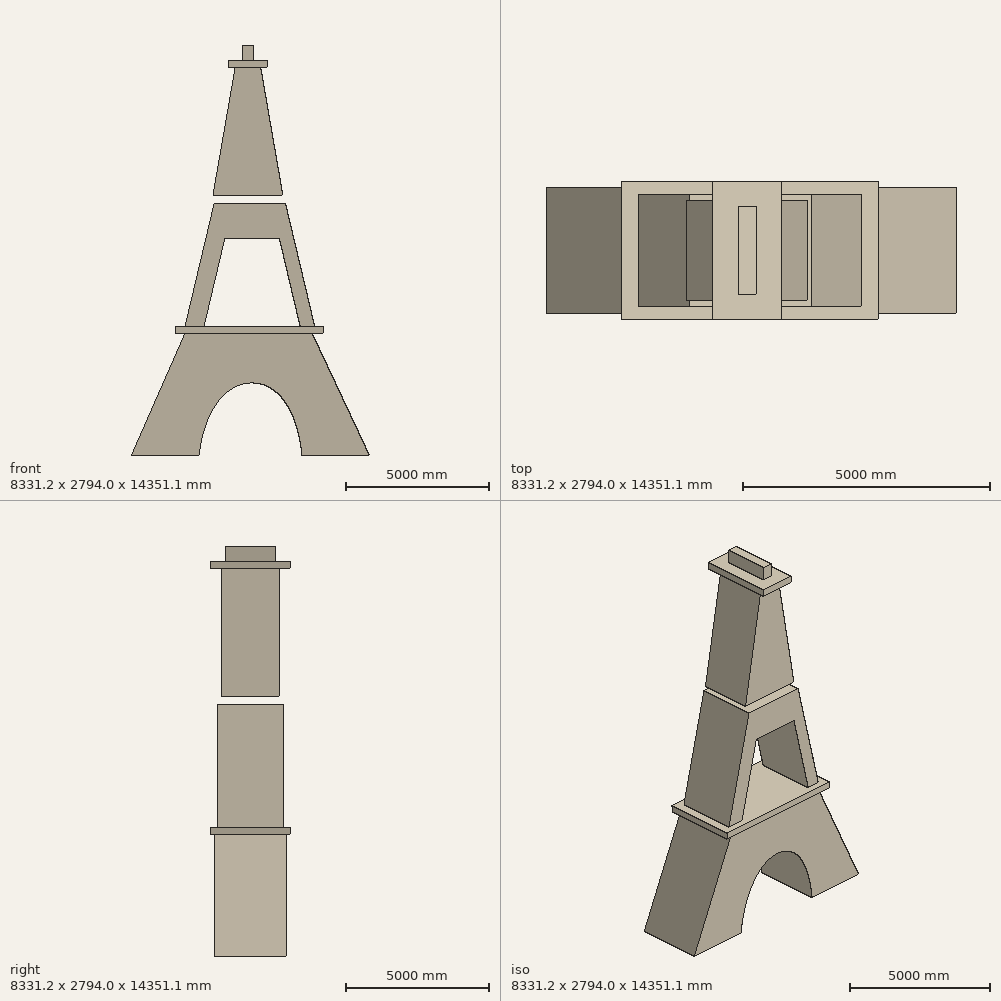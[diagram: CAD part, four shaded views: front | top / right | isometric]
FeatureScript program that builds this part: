
annotation { "Feature Type Name" : "Feature", "Feature Type Description" : "" }
export const myFeature = defineFeature(function(context is Context, id is Id, definition is map)
    precondition{}
    {
        {
            var Q0;
            Q0=qCreatedBy(makeId("Front.planeOp"),FACE);
            var sketch = newSketch(context, id + "F0", { "sketchPlane" : qUnion([Q0])});
            skLineSegment(sketch, "E0", {"start": v(0, 0) * mm, "end": v(-2362.2, 0) * mm});
            skLineSegment(sketch, "E1", {"start": v(3606.8, 0) * mm, "end": v(5969, 0) * mm});
            skFitSpline(sketch, "E2", {"points": [v(0, 0) * mm, v(1882.5, 2540) * mm, v(3606.8, 0) * mm], "startDerivative": vector(1303.2, 10552.75) * mm, "endDerivative": vector(1103.96, -10584.22) * mm});
            skLineSegment(sketch, "E3", {"start": v(-2362.2, 0) * mm, "end": v(-461.9, 4325.37) * mm});
            skLineSegment(sketch, "E4", {"start": v(-483.25, 4276.79) * mm, "end": v(3961.75, 4276.79) * mm});
            skLineSegment(sketch, "E5", {"start": v(3961.75, 4276.79) * mm, "end": v(5969, 0) * mm});
            skLineSegment(sketch, "E6", {"start": v(-832.7, 4530.55) * mm, "end": v(4374.3, 4530.55) * mm});
            skLineSegment(sketch, "E7", {"start": v(4374.3, 4530.55) * mm, "end": v(4374.3, 4276.79) * mm});
            skLineSegment(sketch, "E8", {"start": v(4374.3, 4276.79) * mm, "end": v(3961.75, 4276.79) * mm});
            skLineSegment(sketch, "E9", {"start": v(-483.25, 4276.79) * mm, "end": v(-821.6, 4276.79) * mm});
            skLineSegment(sketch, "E10", {"start": v(-821.6, 4276.79) * mm, "end": v(-832.7, 4530.55) * mm});
            skLineSegment(sketch, "E11", {"start": v(-483.25, 4530.55) * mm, "end": v(536.71, 8830.84) * mm});
            skLineSegment(sketch, "E12", {"start": v(4047.99, 4530.55) * mm, "end": v(3025.91, 8830.34) * mm});
            skLineSegment(sketch, "E13", {"start": v(536.71, 8830.84) * mm, "end": v(3025.91, 8830.34) * mm});
            skLineSegment(sketch, "E14", {"start": v(536.71, 8830.84) * mm, "end": v(0, 8830.95) * mm});
            skLineSegment(sketch, "E15", {"start": v(0, 8830.95) * mm, "end": v(0.05, 9084.95) * mm});
            skLineSegment(sketch, "E16", {"start": v(0.05, 9084.95) * mm, "end": v(3533.96, 9084.24) * mm});
            skLineSegment(sketch, "E17", {"start": v(3025.91, 8830.34) * mm, "end": v(3533.91, 8830.24) * mm});
            skLineSegment(sketch, "E18", {"start": v(3533.91, 8830.24) * mm, "end": v(3533.96, 9084.24) * mm});
            skLineSegment(sketch, "E19", {"start": v(486.63, 9084.85) * mm, "end": v(1270.63, 13589.13) * mm});
            skLineSegment(sketch, "E20", {"start": v(2940.79, 9084.36) * mm, "end": v(2159.63, 13589.13) * mm});
            skLineSegment(sketch, "E21", {"start": v(2159.63, 13589.13) * mm, "end": v(1270.63, 13589.13) * mm});
            skLineSegment(sketch, "E22", {"start": v(1270.63, 13589.13) * mm, "end": v(1016.58, 13589.18) * mm});
            skLineSegment(sketch, "E23", {"start": v(1016.58, 13589.18) * mm, "end": v(1016.63, 13843.18) * mm});
            skLineSegment(sketch, "E24", {"start": v(1016.63, 13843.18) * mm, "end": v(2413.63, 13842.9) * mm});
            skLineSegment(sketch, "E25", {"start": v(2413.63, 13842.9) * mm, "end": v(2413.63, 13589.13) * mm});
            skLineSegment(sketch, "E26", {"start": v(2413.63, 13589.13) * mm, "end": v(2159.63, 13589.13) * mm});
            skLineSegment(sketch, "E27", {"start": v(1913.75, 13843) * mm, "end": v(1913.85, 14351) * mm});
            skLineSegment(sketch, "E28", {"start": v(1532.75, 13843.08) * mm, "end": v(1532.85, 14351.08) * mm});
            skLineSegment(sketch, "E29", {"start": v(1532.85, 14351.08) * mm, "end": v(1913.85, 14351) * mm});
            skLineSegment(sketch, "E30", {"start": v(182.46, 4530.55) * mm, "end": v(909.58, 7596.19) * mm});
            skLineSegment(sketch, "E31", {"start": v(909.58, 7596.19) * mm, "end": v(2814.58, 7596.19) * mm});
            skLineSegment(sketch, "E32", {"start": v(2814.58, 7596.19) * mm, "end": v(3536.95, 4530.55) * mm});
            skPoint(sketch, "E32.endSnap0", {"position": v(3536.95, 6680.44) * mm});
            skSolve(sketch);
        }
        {
            var Q0;
            {var subQ1=sQuery(id+"F0.wireOp",EDGE,"E0");Q0=makeQuery(id+"F0.imprint","IMPRINT",FACE,{"disambiguationData":[TD([[makeQuery(id+"F0.imprint","IMPRINT",EDGE,{"derivedFrom":subQ1}),-1.0]])]});}
            extrude(context, id + "F1", {"entities" : qUnion([Q0]), "endBound" : BoundingType.SYMMETRIC, "depth" : 2540 * mm, "offsetDistance" : 25.4 * mm});
        }
        {
            var Q0;
            {var subQ2=sQuery(id+"F0.wireOp",EDGE,"E11");Q0=makeQuery(id+"F0.imprint","IMPRINT",FACE,{"disambiguationData":[TD([[makeQuery(id+"F0.imprint","IMPRINT",EDGE,{"derivedFrom":subQ2}),-1.0]])]});}
            extrude(context, id + "F2", {"entities" : qUnion([Q0]), "endBound" : BoundingType.SYMMETRIC, "depth" : 2286 * mm, "offsetDistance" : 25.4 * mm});
        }
        {
            var Q0;
            {var subQ0=sQuery(id+"F0.wireOp",EDGE,"E19");Q0=makeQuery(id+"F0.imprint","IMPRINT",FACE,{"disambiguationData":[TD([[makeQuery(id+"F0.imprint","IMPRINT",EDGE,{"derivedFrom":subQ0}),-1.0]])]});}
            extrude(context, id + "F3", {"entities" : qUnion([Q0]), "endBound" : BoundingType.SYMMETRIC, "depth" : 2032 * mm, "offsetDistance" : 25.4 * mm});
        }
        {
            var Q0;
            Q0=makeQuery(id+"F0.imprint","IMPRINT",FACE,{"disambiguationData":[TD([[makeQuery(id+"F0.imprint","IMPRINT",EDGE,{"derivedFrom":sQuery(id+"F0.wireOp",EDGE,"E13")}),1.0]])]});
            var Q1;
            Q1=makeQuery(id+"F0.imprint","IMPRINT",FACE,{"disambiguationData":[TD([[makeQuery(id+"F0.imprint","IMPRINT",EDGE,{"derivedFrom":sQuery(id+"F0.wireOp",EDGE,"E4")}),1.0]])]});
            var Q2;
            Q2=makeQuery(id+"F0.imprint","IMPRINT",FACE,{"disambiguationData":[TD([[makeQuery(id+"F0.imprint","IMPRINT",EDGE,{"derivedFrom":sQuery(id+"F0.wireOp",EDGE,"E21")}),-1.0]])]});
            extrude(context, id + "F4", {"entities" : qUnion([Q0, Q1, Q2]), "endBound" : BoundingType.SYMMETRIC, "depth" : 2794 * mm, "offsetDistance" : 25.4 * mm});
        }
        {
            var Q0;
            {var subQ0=sQuery(id+"F0.wireOp",EDGE,"E27");Q0=makeQuery(id+"F0.imprint","IMPRINT",FACE,{"disambiguationData":[TD([[makeQuery(id+"F0.imprint","IMPRINT",EDGE,{"derivedFrom":subQ0}),1.0]])]});}
            extrude(context, id + "F5", {"entities" : qUnion([Q0]), "operationType" : NewBodyOperationType.ADD, "endBound" : BoundingType.SYMMETRIC, "depth" : 1778 * mm, "offsetDistance" : 25.4 * mm});
        }
    });
